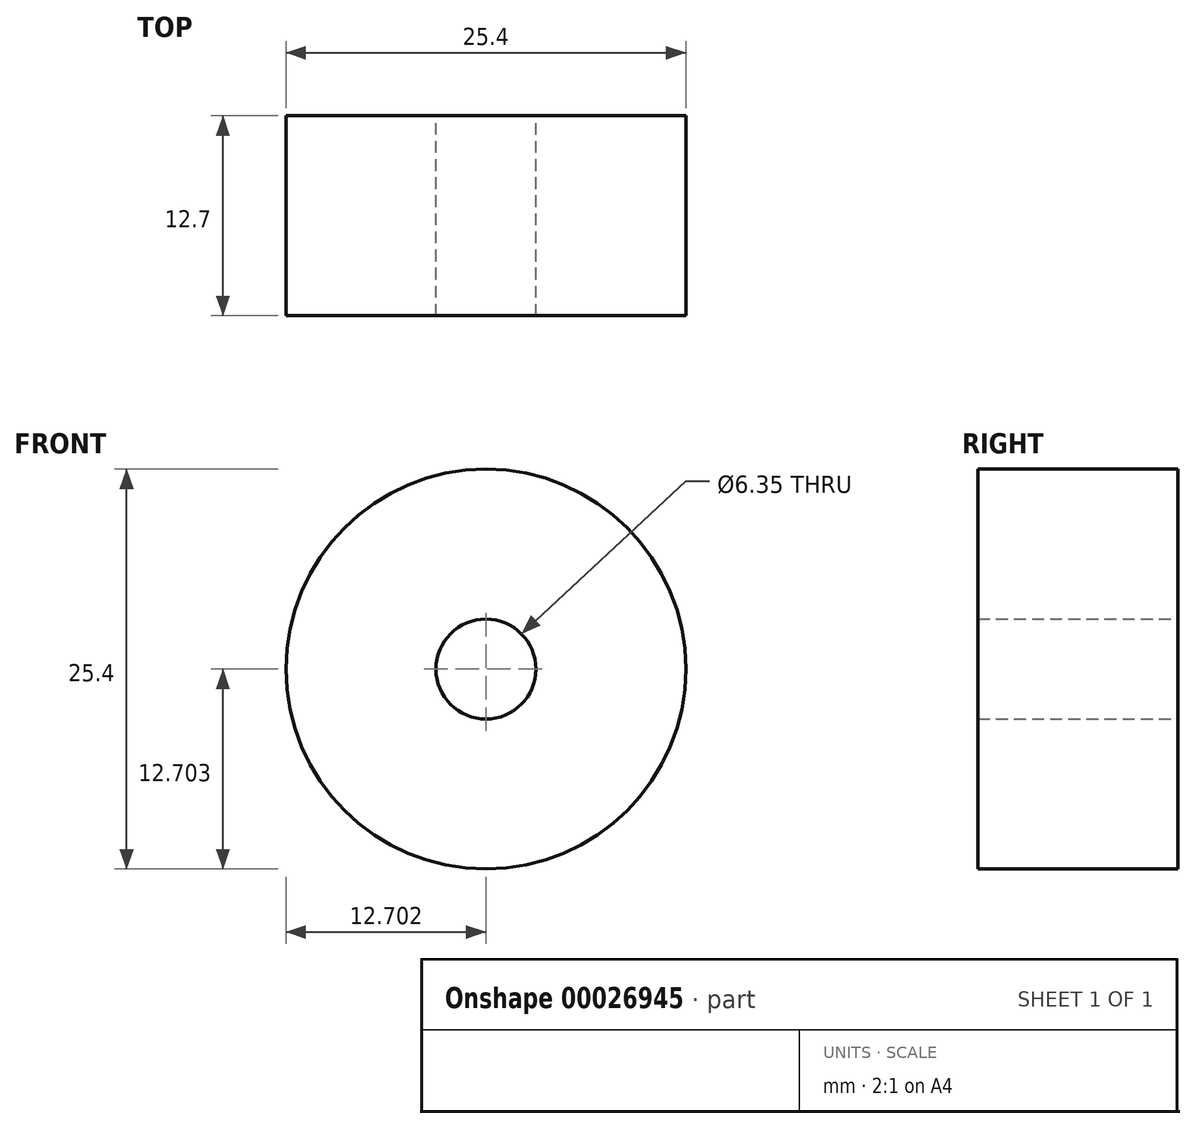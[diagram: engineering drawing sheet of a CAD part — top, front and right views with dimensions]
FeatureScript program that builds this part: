
annotation { "Feature Type Name" : "Feature", "Feature Type Description" : "" }
export const myFeature = defineFeature(function(context is Context, id is Id, definition is map)
    precondition{}
    {
        {
            var Q0;
            Q0=qCreatedBy(makeId("Front.planeOp"),FACE);
            var sketch = newSketch(context, id + "F0", { "sketchPlane" : qUnion([Q0])});
            skCircle(sketch, "E0", {"center": v(-36.98, 26.34) * mm, "radius": 12.7 * mm});
            skCircle(sketch, "E1", {"center": v(-36.98, 26.34) * mm, "radius": 3.18 * mm});
            skSolve(sketch);
        }
        {
            var Q0;
            Q0=makeQuery(id+"F0.imprint","IMPRINT",FACE,{"disambiguationData":[TD([[makeQuery(id+"F0.imprint","IMPRINT",EDGE,{"derivedFrom":sQuery(id+"F0.wireOp",EDGE,"E0")}),1.0]])]});
            extrude(context, id + "F1", {"entities" : qUnion([Q0]), "depth" : 12.7 * mm});
        }
    });
